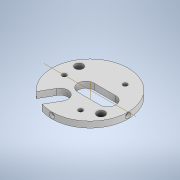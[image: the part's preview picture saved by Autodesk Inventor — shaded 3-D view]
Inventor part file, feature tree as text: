
AUTODESK INVENTOR PART (.ipt)
format: ipt  version: 2021 (Build 250183000, 183)  size: 181,248 bytes
history: native  units: in
note: dims shown in document units (in); Inventor stores cm internally (conversion verified against a paired STEP export)
features: plane x2, other x2, extrude x1, hole x1, pattern_circular x1, sketch x1
ambient origin geometry x8: Origin, YZ Plane, XZ Plane, XY Plane, X Axis, Y Axis, Z Axis, Center Point
bodies: Solid1 (feature_tree)
feature tree (8):
  extrude  "Extrusion1"  TaperAngle=60.0deg  [1 undecoded]
  plane  "Work Plane2"
  hole  "Hole1"  [1 undecoded]
  other  "Work Axis2"
  pattern_circular  "Circular Pattern1"  Angle=30.0deg  [1 undecoded]
  other  "Work Axis1"
  plane  "Work Plane1"
  sketch  "Sketch2"  dims[d0=4.75in d1=60.0deg d2=120.0deg d3=30.0deg d10=3.75in d12=2.76in d14=3.2165in d16=1.1811in d18=360.0deg d20=0.7874in d22=360.0deg d25=0.0in d26=0.25in d27=1.358in d28=1.0in d29=1.0in d31=0.0in d32=0.19in d33=0.13in d34=0.328in d35=0.332in d36=0.25in d37=0.5635in d38=0.484in d39=0.8108in d40=1.5748in d41=360.0deg d42=0.0625in d43=0.75in d44=0.375in]
note: 3 required parameter values undecoded (feature->parameter linkage not recoverable at this tier; creation-order binding heuristic only, values carry confidence <= 0.55)
